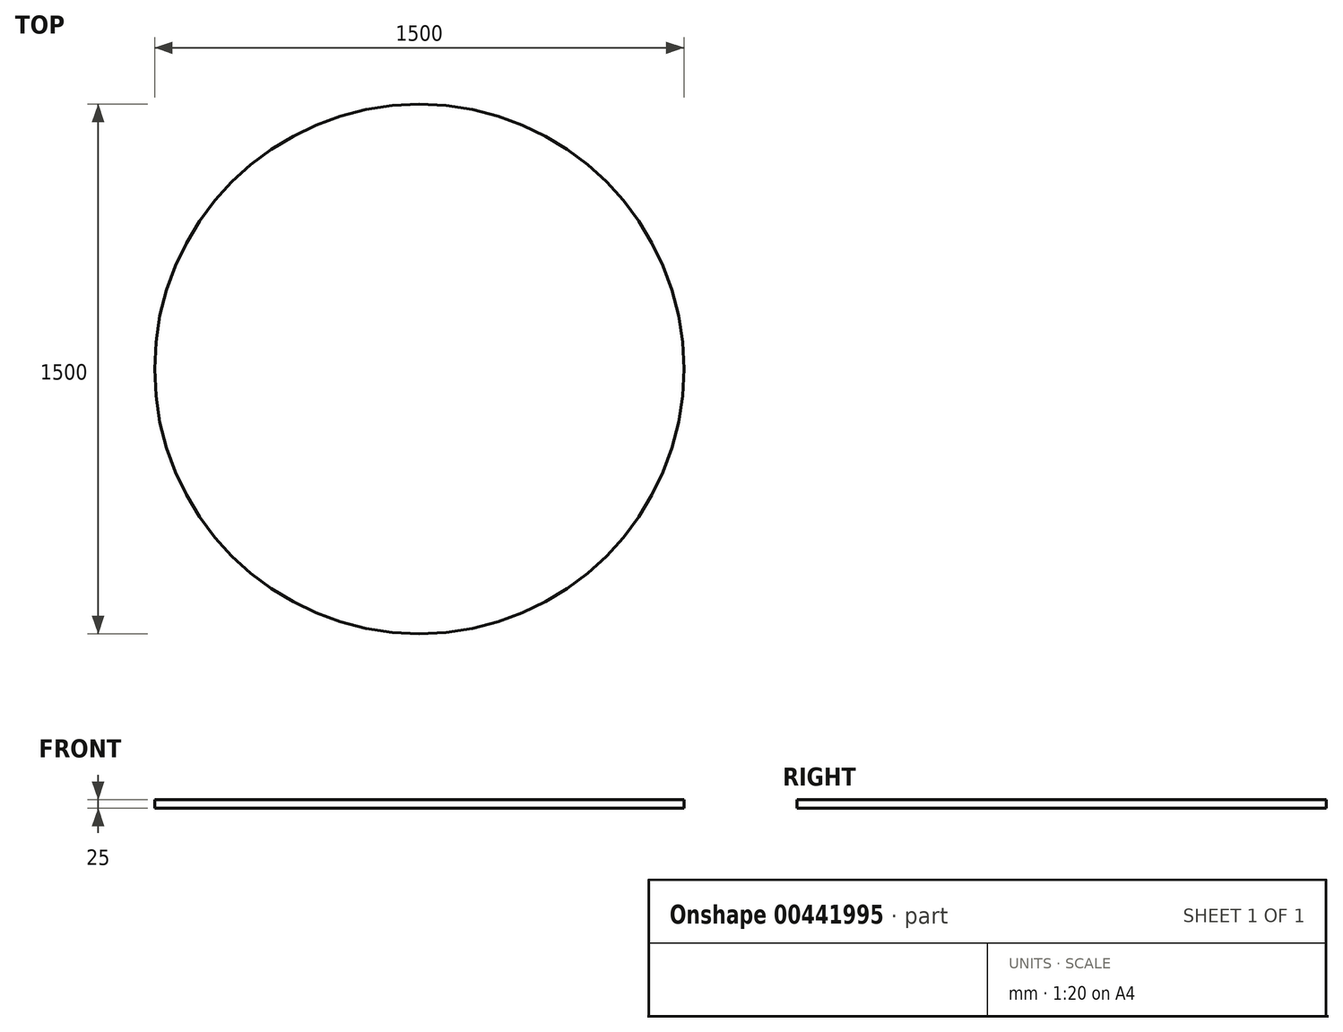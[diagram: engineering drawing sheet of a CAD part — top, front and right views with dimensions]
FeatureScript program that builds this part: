
annotation { "Feature Type Name" : "Feature", "Feature Type Description" : "" }
export const myFeature = defineFeature(function(context is Context, id is Id, definition is map)
    precondition{}
    {
        {
            var Q0;
            Q0=qCreatedBy(makeId("Top.planeOp"),FACE);
            var sketch = newSketch(context, id + "F0", { "sketchPlane" : qUnion([Q0])});
            skCircle(sketch, "E0", {"center": v(0, 0) * mm, "radius": 750 * mm});
            skSolve(sketch);
        }
        {
            var Q0;
            Q0 = qSketchRegion(id + "F0", true);
            extrude(context, id + "F1", {"entities" : qUnion([Q0]), "depth" : 25 * mm});
        }
    });
